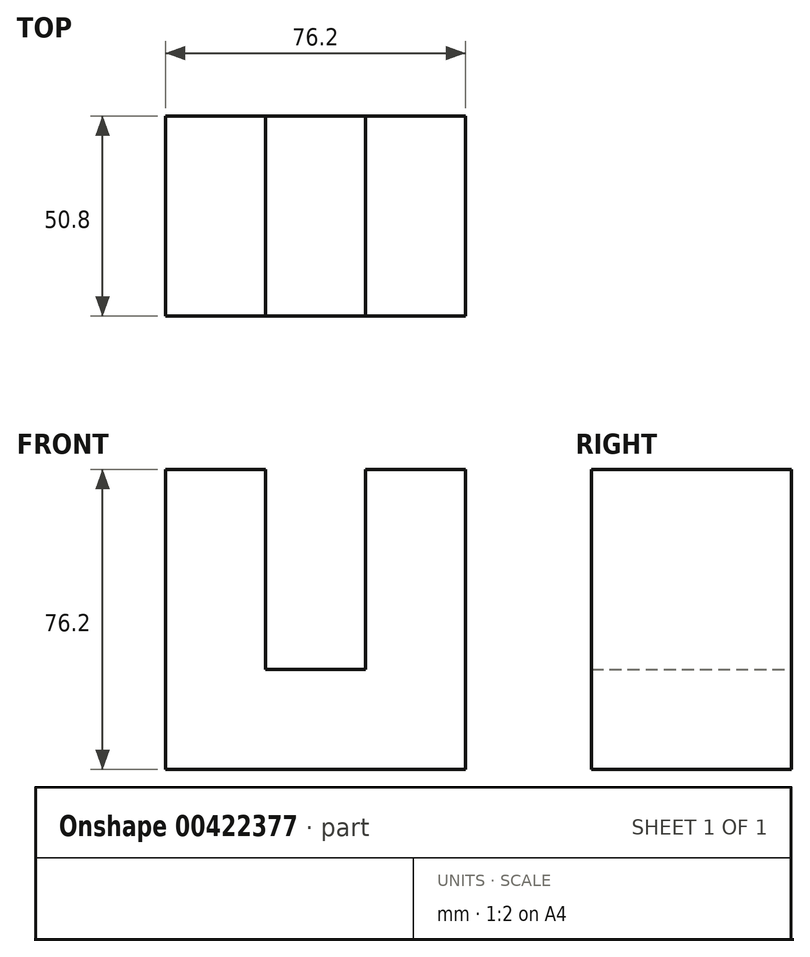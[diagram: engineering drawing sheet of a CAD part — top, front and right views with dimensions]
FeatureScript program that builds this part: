
annotation { "Feature Type Name" : "Feature", "Feature Type Description" : "" }
export const myFeature = defineFeature(function(context is Context, id is Id, definition is map)
    precondition{}
    {
        {
            var Q0;
            Q0=qCreatedBy(makeId("Front.planeOp"),FACE);
            var sketch = newSketch(context, id + "F0", { "sketchPlane" : qUnion([Q0])});
            skLineSegment(sketch, "E0", {"start": v(-48.7, 28.27) * mm, "end": v(-48.7, -47.93) * mm});
            skLineSegment(sketch, "E1", {"start": v(-48.7, -47.93) * mm, "end": v(27.5, -47.93) * mm});
            skLineSegment(sketch, "E2", {"start": v(27.5, -47.93) * mm, "end": v(27.5, 28.27) * mm});
            skLineSegment(sketch, "E3", {"start": v(27.5, 28.27) * mm, "end": v(2.1, 28.27) * mm});
            skLineSegment(sketch, "E4", {"start": v(2.1, 28.27) * mm, "end": v(2.1, -22.53) * mm});
            skLineSegment(sketch, "E5", {"start": v(2.1, -22.53) * mm, "end": v(-23.3, -22.53) * mm});
            skLineSegment(sketch, "E6", {"start": v(-23.3, -22.53) * mm, "end": v(-23.3, 28.27) * mm});
            skLineSegment(sketch, "E7", {"start": v(-23.3, 28.27) * mm, "end": v(-48.7, 28.27) * mm});
            skSolve(sketch);
        }
        {
            var Q0;
            Q0 = qSketchRegion(id + "F0", true);
            extrude(context, id + "F1", {"entities" : qUnion([Q0]), "depth" : 50.8 * mm});
        }
    });
